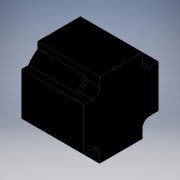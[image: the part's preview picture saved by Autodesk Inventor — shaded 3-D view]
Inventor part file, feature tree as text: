
AUTODESK INVENTOR PART (.ipt)
format: ipt  version: 2019 (Build 230136000, 136)  size: 139,776 bytes
history: native  units: mm
features: other x14, extrude x2, sketch x2
ambient origin geometry x8: Origin, YZ Plane, XZ Plane, XY Plane, X Axis, Y Axis, Z Axis, Center Point
bodies: Solid1 (feature_tree)
feature tree (18):
  extrude  "Extrusion1"  Depth=74.0mm TaperAngle=0.0deg
  extrude  "Extrusion2"  [1 undecoded]
  other  "H1_XY"
  other  "H1_YZ"
  other  "H1_ZX"
  other  "H1_X"
  other  "H1_Y"
  other  "H1_Z"
  other  "H1_Center"
  other  "H2_XY"
  other  "H2_YZ"
  other  "H2_ZX"
  other  "H2_X"
  other  "H2_Y"
  other  "H2_Z"
  other  "H2_Center"
  sketch  "Sketch_1"  dims[d0=94.0mm d1=0.0mm d2=74.0mm d3=0.0mm]
  sketch  "Sketch_2"  dims[d4=0.0mm d5=0.0mm]
note: 1 required parameter value undecoded (feature->parameter linkage not recoverable at this tier; creation-order binding heuristic only, values carry confidence <= 0.55)
